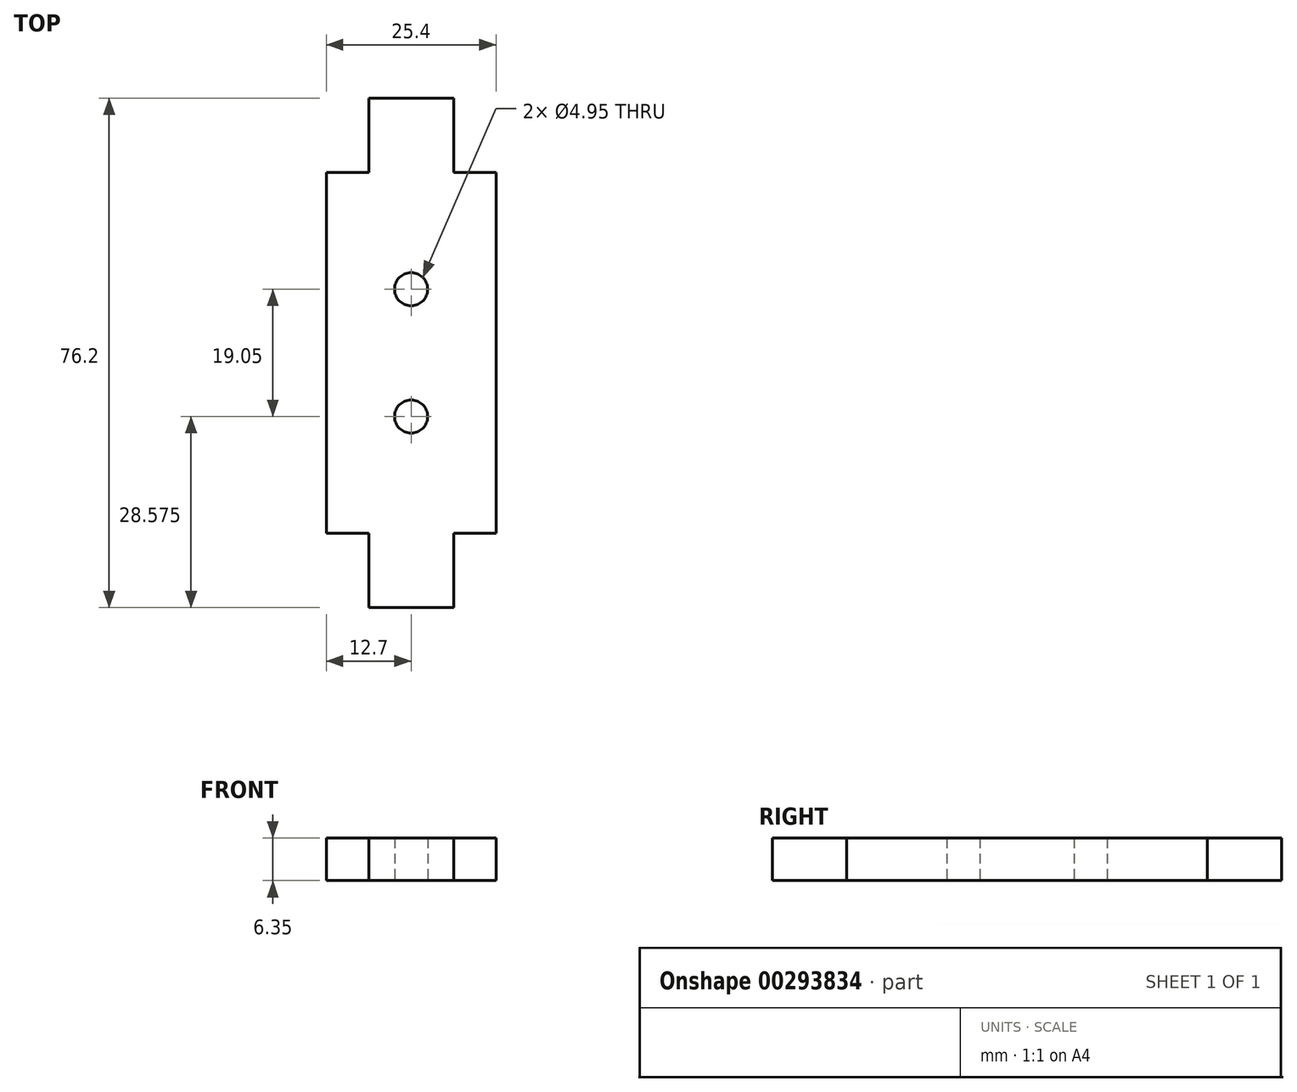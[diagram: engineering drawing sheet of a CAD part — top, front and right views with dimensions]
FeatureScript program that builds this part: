
annotation { "Feature Type Name" : "Feature", "Feature Type Description" : "" }
export const myFeature = defineFeature(function(context is Context, id is Id, definition is map)
    precondition{}
    {
        {
            var Q0;
            Q0=qCreatedBy(makeId("Top.planeOp"),FACE);
            var sketch = newSketch(context, id + "F0", { "sketchPlane" : qUnion([Q0])});
            skLineSegment(sketch, "E0.bottom", {"start": v(12.7, -26.99) * mm, "end": v(6.35, -26.99) * mm});
            skLineSegment(sketch, "E0.top", {"start": v(12.7, 26.99) * mm, "end": v(6.35, 26.99) * mm});
            skLineSegment(sketch, "E0.left", {"start": v(12.7, -26.99) * mm, "end": v(12.7, 26.99) * mm});
            skLineSegment(sketch, "E0.right", {"start": v(-12.7, -26.99) * mm, "end": v(-12.7, 26.99) * mm});
            skPoint(sketch, "E0.middle", {"position": v(0, 0) * mm});
            skLineSegment(sketch, "E1.top", {"start": v(6.35, 38.1) * mm, "end": v(-6.35, 38.1) * mm});
            skLineSegment(sketch, "E1.left", {"start": v(6.35, 26.99) * mm, "end": v(6.35, 38.1) * mm});
            skLineSegment(sketch, "E1.right", {"start": v(-6.35, 26.99) * mm, "end": v(-6.35, 38.1) * mm});
            skPoint(sketch, "E1.middle", {"position": v(0, 32.54) * mm});
            skLineSegment(sketch, "E2.top", {"start": v(6.35, -38.1) * mm, "end": v(-6.35, -38.1) * mm});
            skLineSegment(sketch, "E2.left", {"start": v(6.35, -26.99) * mm, "end": v(6.35, -38.1) * mm});
            skLineSegment(sketch, "E2.right", {"start": v(-6.35, -26.99) * mm, "end": v(-6.35, -38.1) * mm});
            skPoint(sketch, "E2.middle", {"position": v(0, -32.54) * mm});
            skPoint(sketch, "E2.middle.positionSnap0", {"position": v(0, -26.99) * mm});
            skPoint(sketch, "E2.centerSnap0", {"position": v(0, -26.99) * mm});
            skLineSegment(sketch, "E3.trimOffspring", {"start": v(-6.35, 26.99) * mm, "end": v(-12.7, 26.99) * mm});
            skLineSegment(sketch, "E4.trimOffspring", {"start": v(-6.35, -26.99) * mm, "end": v(-12.7, -26.99) * mm});
            skCircle(sketch, "E5", {"center": v(0, 9.53) * mm, "radius": 2.48 * mm});
            skCircle(sketch, "E6", {"center": v(0, -9.53) * mm, "radius": 2.48 * mm});
            skSolve(sketch);
        }
        {
            var Q0;
            Q0 = qSketchRegion(id + "F0", true);
            extrude(context, id + "F1", {"entities" : qUnion([Q0]), "depth" : 6.35 * mm});
        }
    });
